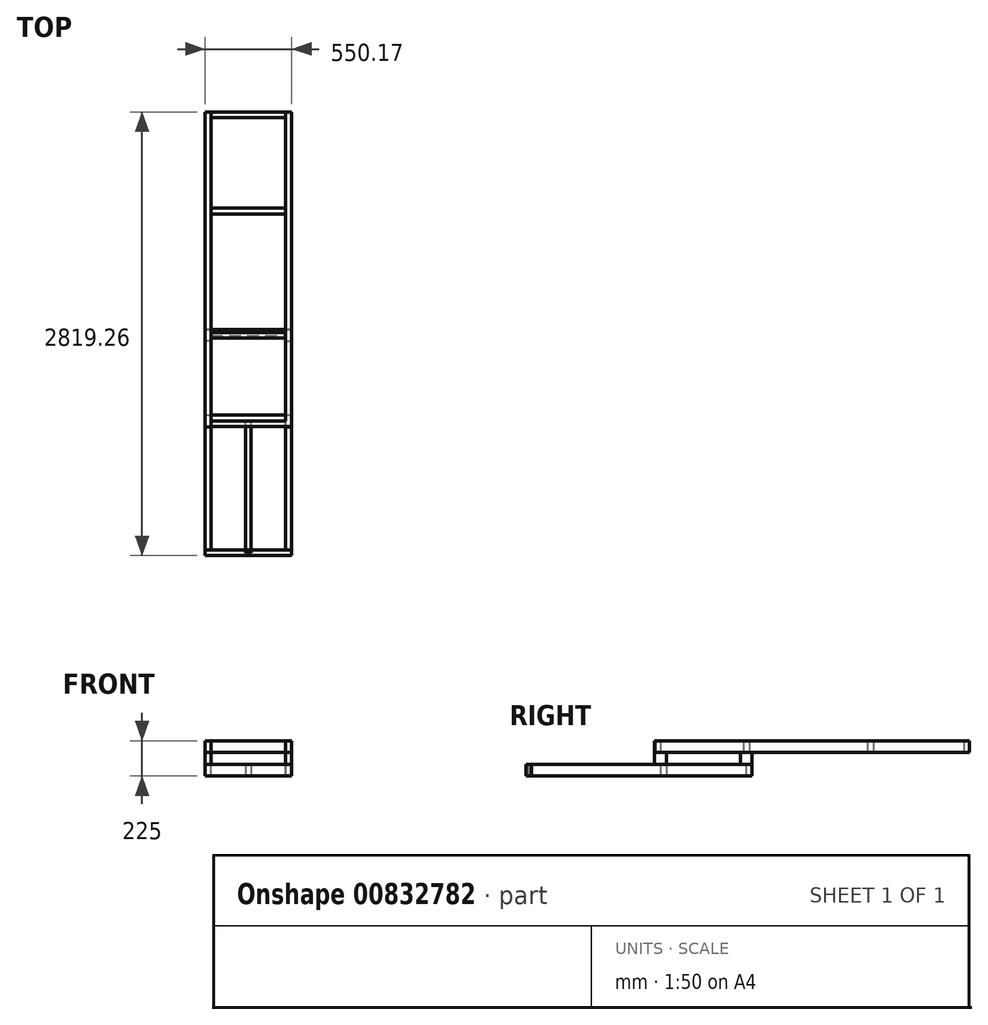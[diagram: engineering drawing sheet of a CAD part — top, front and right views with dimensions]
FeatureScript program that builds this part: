
annotation { "Feature Type Name" : "Feature", "Feature Type Description" : "" }
export const myFeature = defineFeature(function(context is Context, id is Id, definition is map)
    precondition{}
    {
        {
            var Q0;
            Q0=qCreatedBy(makeId("Top.planeOp"),FACE);
            var sketch = newSketch(context, id + "F0", { "sketchPlane" : qUnion([Q0])});
            skLineSegment(sketch, "E0.bottom", {"start": v(33.92, 1002.77) * mm, "end": v(71.42, 1002.77) * mm});
            skLineSegment(sketch, "E0.top", {"start": v(33.92, -997.23) * mm, "end": v(71.42, -997.23) * mm});
            skLineSegment(sketch, "E0.left", {"start": v(33.92, 1002.77) * mm, "end": v(33.92, -997.23) * mm});
            skLineSegment(sketch, "E0.right", {"start": v(71.42, 1002.77) * mm, "end": v(71.42, -997.23) * mm});
            skLineSegment(sketch, "E1.bottom", {"start": v(-478.58, 1002.64) * mm, "end": v(-441.08, 1002.64) * mm});
            skLineSegment(sketch, "E1.top", {"start": v(-478.58, -997.36) * mm, "end": v(-441.08, -997.36) * mm});
            skLineSegment(sketch, "E1.left", {"start": v(-478.58, 1002.64) * mm, "end": v(-478.58, -997.36) * mm});
            skLineSegment(sketch, "E1.right", {"start": v(-441.08, 1002.64) * mm, "end": v(-441.08, -997.36) * mm});
            skSolve(sketch);
        }
        {
            var Q0;
            Q0=qCreatedBy(makeId("Top.planeOp"),FACE);
            var sketch = newSketch(context, id + "F1", { "sketchPlane" : qUnion([Q0])});
            skLineSegment(sketch, "E2.bottom", {"start": v(33.8, 1002.83) * mm, "end": v(-441.2, 1002.83) * mm});
            skLineSegment(sketch, "E2.top", {"start": v(33.8, 965.33) * mm, "end": v(-441.2, 965.33) * mm});
            skLineSegment(sketch, "E2.left", {"start": v(33.8, 1002.83) * mm, "end": v(33.8, 965.33) * mm});
            skLineSegment(sketch, "E2.right", {"start": v(-441.2, 1002.83) * mm, "end": v(-441.2, 965.33) * mm});
            skLineSegment(sketch, "E3.bottom", {"start": v(-441.4, 390.33) * mm, "end": v(33.6, 390.33) * mm});
            skLineSegment(sketch, "E3.top", {"start": v(-441.4, 352.83) * mm, "end": v(33.6, 352.83) * mm});
            skLineSegment(sketch, "E3.left", {"start": v(-441.4, 390.33) * mm, "end": v(-441.4, 352.83) * mm});
            skLineSegment(sketch, "E3.right", {"start": v(33.6, 390.33) * mm, "end": v(33.6, 352.83) * mm});
            skLineSegment(sketch, "E4.bottom", {"start": v(34.02, -997.33) * mm, "end": v(-440.98, -997.33) * mm});
            skLineSegment(sketch, "E4.top", {"start": v(34.02, -959.83) * mm, "end": v(-440.98, -959.83) * mm});
            skLineSegment(sketch, "E4.left", {"start": v(34.02, -997.33) * mm, "end": v(34.02, -959.83) * mm});
            skLineSegment(sketch, "E4.right", {"start": v(-440.98, -997.33) * mm, "end": v(-440.98, -959.83) * mm});
            skLineSegment(sketch, "E5.bottom", {"start": v(-441.15, -397.33) * mm, "end": v(33.85, -397.33) * mm});
            skLineSegment(sketch, "E5.top", {"start": v(-441.15, -434.83) * mm, "end": v(33.85, -434.83) * mm});
            skLineSegment(sketch, "E5.left", {"start": v(-441.15, -397.33) * mm, "end": v(-441.15, -434.83) * mm});
            skLineSegment(sketch, "E5.right", {"start": v(33.85, -397.33) * mm, "end": v(33.85, -434.83) * mm});
            skSolve(sketch);
        }
        {
            var Q0;
            Q0=qSketchRegion(id+"F0",true);
            var Q1;
            Q1=qSketchRegion(id+"F1",true);
            extrude(context, id + "F2", {"entities" : qUnion([Q0, Q1]), "depth" : 75 * mm, "offsetDistance" : 25 * mm});
        }
        {
            var Q0;
            Q0=qCreatedBy(makeId("Top.planeOp"),FACE);
            var sketch = newSketch(context, id + "F3", { "sketchPlane" : qUnion([Q0])});
            skLineSegment(sketch, "E6.bottom", {"start": v(-441.28, -378.95) * mm, "end": v(-478.72, -378.95) * mm});
            skLineSegment(sketch, "E6.top", {"start": v(-441.28, -453.95) * mm, "end": v(-478.72, -453.95) * mm});
            skLineSegment(sketch, "E6.left", {"start": v(-441.28, -378.95) * mm, "end": v(-441.28, -453.95) * mm});
            skLineSegment(sketch, "E6.right", {"start": v(-478.72, -378.95) * mm, "end": v(-478.72, -453.95) * mm});
            skLineSegment(sketch, "E7.bottom", {"start": v(-478.47, -997.56) * mm, "end": v(-441.12, -997.56) * mm});
            skLineSegment(sketch, "E7.top", {"start": v(-478.47, -922.56) * mm, "end": v(-441.12, -922.56) * mm});
            skLineSegment(sketch, "E7.left", {"start": v(-478.47, -997.56) * mm, "end": v(-478.47, -922.56) * mm});
            skLineSegment(sketch, "E7.right", {"start": v(-441.12, -997.56) * mm, "end": v(-441.12, -922.56) * mm});
            skLineSegment(sketch, "E8.bottom", {"start": v(33.97, -998) * mm, "end": v(71.4, -998) * mm});
            skLineSegment(sketch, "E8.top", {"start": v(33.97, -923) * mm, "end": v(71.4, -923) * mm});
            skLineSegment(sketch, "E8.left", {"start": v(33.97, -998) * mm, "end": v(33.97, -923) * mm});
            skLineSegment(sketch, "E8.right", {"start": v(71.4, -998) * mm, "end": v(71.4, -923) * mm});
            skLineSegment(sketch, "E9.bottom", {"start": v(33.98, -454.18) * mm, "end": v(71.37, -454.18) * mm});
            skLineSegment(sketch, "E9.top", {"start": v(33.98, -379.18) * mm, "end": v(71.37, -379.18) * mm});
            skLineSegment(sketch, "E9.left", {"start": v(33.98, -454.18) * mm, "end": v(33.98, -379.18) * mm});
            skLineSegment(sketch, "E9.right", {"start": v(71.37, -454.18) * mm, "end": v(71.37, -379.18) * mm});
            skSolve(sketch);
        }
        {
            var Q0;
            Q0 = qSketchRegion(id + "F3", true);
            extrude(context, id + "F4", {"entities" : qUnion([Q0]), "operationType" : NewBodyOperationType.ADD, "oppositeDirection" : true, "depth" : 75 * mm, "offsetDistance" : 25 * mm});
        }
        {
            var Q0;
            Q0=makeQuery(id+"F4.opExtrude","CAP_FACE",FACE,{"disambiguationData":[OSD([sQuery(id+"F3.wireOp",EDGE,"E7.bottom"),sQuery(id+"F3.wireOp",EDGE,"E7.top"),sQuery(id+"F3.wireOp",EDGE,"E7.left"),sQuery(id+"F3.wireOp",EDGE,"E7.right")])],"isStart":false});
            var sketch = newSketch(context, id + "F5", { "sketchPlane" : qUnion([Q0])});
            skLineSegment(sketch, "E10.bottom", {"start": v(-478.62, 378.93) * mm, "end": v(-441.12, 378.93) * mm});
            skLineSegment(sketch, "E10.top", {"start": v(-478.62, 1778.93) * mm, "end": v(-441.12, 1778.93) * mm});
            skLineSegment(sketch, "E10.left", {"start": v(-478.62, 378.93) * mm, "end": v(-478.62, 1778.93) * mm});
            skLineSegment(sketch, "E10.right", {"start": v(-441.12, 378.93) * mm, "end": v(-441.12, 1778.93) * mm});
            skLineSegment(sketch, "E11.bottom", {"start": v(71.4, 379.2) * mm, "end": v(33.9, 379.2) * mm});
            skLineSegment(sketch, "E11.top", {"start": v(71.4, 1779.2) * mm, "end": v(33.9, 1779.2) * mm});
            skLineSegment(sketch, "E11.left", {"start": v(71.4, 379.2) * mm, "end": v(71.4, 1779.2) * mm});
            skLineSegment(sketch, "E11.right", {"start": v(33.9, 379.2) * mm, "end": v(33.9, 1779.2) * mm});
            skSolve(sketch);
        }
        {
            var Q0;
            {var subQ2=sQuery(id+"F5.wireOp",EDGE,"E10.bottom");Q0=makeQuery(id+"F5.imprint","IMPRINT",FACE,{"disambiguationData":[TD([[makeQuery(id+"F5.imprint","IMPRINT",EDGE,{"derivedFrom":subQ2}),1.0]])]});}
            var Q1;
            {var subQ1=makeQuery(id+"F4.opExtrude","CAP_EDGE",EDGE,{"disambiguationData":[OSD([sQuery(id+"F3.wireOp",EDGE,"E7.bottom")])],"isStart":false});Q1=makeQuery(id+"F5.imprint","IMPRINT",FACE,{"disambiguationData":[TD([[makeQuery(id+"F5.imprint","IMPRINT",EDGE,{"derivedFrom":subQ1}),-1.0]])]});}
            extrude(context, id + "F6", {"entities" : qUnion([Q0, Q1]), "operationType" : NewBodyOperationType.ADD, "depth" : 75 * mm, "offsetDistance" : 25 * mm});
        }
        {
            var Q0;
            Q0 = qSketchRegion(id + "F5", true);
            extrude(context, id + "F7", {"entities" : qUnion([Q0]), "depth" : 75 * mm, "offsetDistance" : 25 * mm});
        }
        {
            var Q0;
            Q0=makeQuery(id+"F7.opExtrude","SWEPT_FACE",FACE,{"disambiguationData":[OSD([sQuery(id+"F5.wireOp",EDGE,"E11.right")])]});
            var sketch = newSketch(context, id + "F8", { "sketchPlane" : qUnion([Q0])});
            skLineSegment(sketch, "E12.bottom", {"start": v(379.2, -75) * mm, "end": v(416.7, -75) * mm});
            skLineSegment(sketch, "E12.top", {"start": v(379.2, -150) * mm, "end": v(416.7, -150) * mm});
            skLineSegment(sketch, "E12.left", {"start": v(379.2, -75) * mm, "end": v(379.2, -150) * mm});
            skLineSegment(sketch, "E12.right", {"start": v(416.7, -75) * mm, "end": v(416.7, -150) * mm});
            skSolve(sketch);
        }
        {
            var Q0;
            Q0=makeQuery(id+"F8.imprint","IMPRINT",FACE,{"disambiguationData":[TD([[makeQuery(id+"F8.imprint","IMPRINT",EDGE,{"derivedFrom":sQuery(id+"F8.wireOp",EDGE,"E12.bottom")}),-1.0]])]});
            extrude(context, id + "F9", {"entities" : qUnion([Q0]), "operationType" : NewBodyOperationType.ADD, "depth" : 475 * mm, "offsetDistance" : 25 * mm});
        }
        {
            var Q0;
            Q0=makeQuery(id+"F6.opExtrude","SWEPT_FACE",FACE,{"disambiguationData":[OSD([sQuery(id+"F5.wireOp",EDGE,"E10.top")])]});
            var sketch = newSketch(context, id + "F10", { "sketchPlane" : qUnion([Q0])});
            skLineSegment(sketch, "E13.bottom", {"start": v(-478.62, -75) * mm, "end": v(71.45, -75) * mm});
            skLineSegment(sketch, "E13.top", {"start": v(-478.62, -149.9) * mm, "end": v(71.45, -149.9) * mm});
            skLineSegment(sketch, "E13.left", {"start": v(-478.62, -75) * mm, "end": v(-478.62, -149.9) * mm});
            skLineSegment(sketch, "E13.right", {"start": v(71.45, -75) * mm, "end": v(71.45, -149.9) * mm});
            skSolve(sketch);
        }
        {
            var Q0;
            Q0 = qSketchRegion(id + "F10", true);
            extrude(context, id + "F11", {"entities" : qUnion([Q0]), "depth" : 37.5 * mm, "offsetDistance" : 25 * mm});
        }
        {
            var Q0;
            Q0=makeQuery(id+"F7.opExtrude","SWEPT_FACE",FACE,{"disambiguationData":[OSD([sQuery(id+"F5.wireOp",EDGE,"E10.right")])]});
            var sketch = newSketch(context, id + "F12", { "sketchPlane" : qUnion([Q0])});
            skLineSegment(sketch, "E14.bottom", {"start": v(-922.68, -75) * mm, "end": v(-960.18, -75) * mm});
            skLineSegment(sketch, "E14.top", {"start": v(-922.68, -150) * mm, "end": v(-960.18, -150) * mm});
            skLineSegment(sketch, "E14.left", {"start": v(-922.68, -75) * mm, "end": v(-922.68, -150) * mm});
            skLineSegment(sketch, "E14.right", {"start": v(-960.18, -75) * mm, "end": v(-960.18, -150) * mm});
            skSolve(sketch);
        }
        {
            var Q0;
            Q0=makeQuery(id+"F12.imprint","IMPRINT",FACE,{"disambiguationData":[TD([[makeQuery(id+"F12.imprint","IMPRINT",EDGE,{"derivedFrom":sQuery(id+"F12.wireOp",EDGE,"E14.bottom")}),1.0]])]});
            extrude(context, id + "F13", {"entities" : qUnion([Q0]), "depth" : 475 * mm, "offsetDistance" : 25 * mm});
        }
        {
            var Q0;
            Q0=makeQuery(id+"F13.opExtrude","SWEPT_FACE",FACE,{"disambiguationData":[OSD([sQuery(id+"F12.wireOp",EDGE,"E14.right")])]});
            var sketch = newSketch(context, id + "F14", { "sketchPlane" : qUnion([Q0])});
            skLineSegment(sketch, "E15.bottom", {"start": v(-222.42, -75) * mm, "end": v(-184.82, -75) * mm});
            skLineSegment(sketch, "E15.top", {"start": v(-222.42, -150) * mm, "end": v(-184.82, -150) * mm});
            skLineSegment(sketch, "E15.left", {"start": v(-222.42, -75) * mm, "end": v(-222.42, -150) * mm});
            skLineSegment(sketch, "E15.right", {"start": v(-184.82, -75) * mm, "end": v(-184.82, -150) * mm});
            skSolve(sketch);
        }
        {
            var Q0;
            Q0=makeQuery(id+"F14.imprint","IMPRINT",FACE,{"disambiguationData":[TD([[makeQuery(id+"F14.imprint","IMPRINT",EDGE,{"derivedFrom":sQuery(id+"F14.wireOp",EDGE,"E15.bottom")}),1.0]])]});
            extrude(context, id + "F15", {"entities" : qUnion([Q0]), "depth" : 837.5 * mm, "offsetDistance" : 25 * mm});
        }
    });
